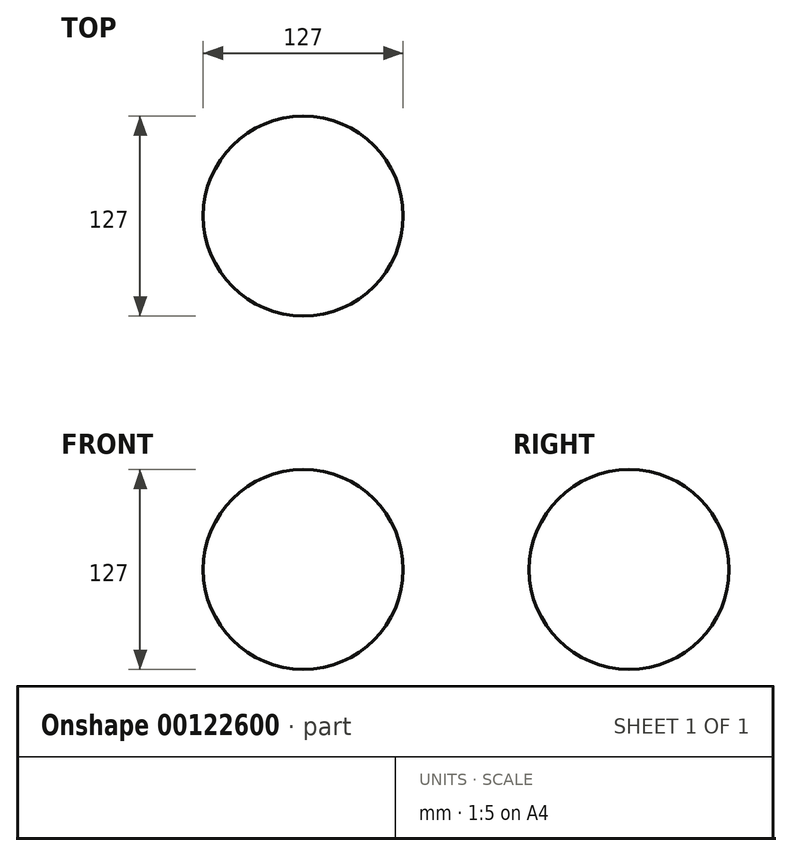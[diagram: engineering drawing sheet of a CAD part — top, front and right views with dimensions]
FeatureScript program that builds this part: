
annotation { "Feature Type Name" : "Feature", "Feature Type Description" : "" }
export const myFeature = defineFeature(function(context is Context, id is Id, definition is map)
    precondition{}
    {
        {
            var Q0;
            Q0=qCreatedBy(makeId("Front.planeOp"),FACE);
            var sketch = newSketch(context, id + "F0", { "sketchPlane" : qUnion([Q0])});
            skArc(sketch, "E0", {"start": v(63.5, 0) * mm, "mid": v(0, 63.5) * mm, "end": v(-63.5, 0) * mm});
            skLineSegment(sketch, "E1", {"start": v(-128.52, 0) * mm, "end": v(130.53, 0) * mm, "construction": true});
            skLineSegment(sketch, "E2", {"start": v(-63.5, 0) * mm, "end": v(63.5, 0) * mm});
            skSolve(sketch);
        }
        {
            var Q0;
            Q0=makeQuery(id+"F0.imprint","IMPRINT",FACE,{"disambiguationData":[TD([[makeQuery(id+"F0.imprint","IMPRINT",EDGE,{"derivedFrom":sQuery(id+"F0.wireOp",EDGE,"E0")}),1.0]])]});
            var Q1;
            Q1=sQuery(id+"F0.wireOp",EDGE,"E1");
            revolve(context, id + "F1", {"entities" : qUnion([Q0]), "axis" : qUnion([Q1]), "revolveType" : RevolveType.FULL});
        }
    });
